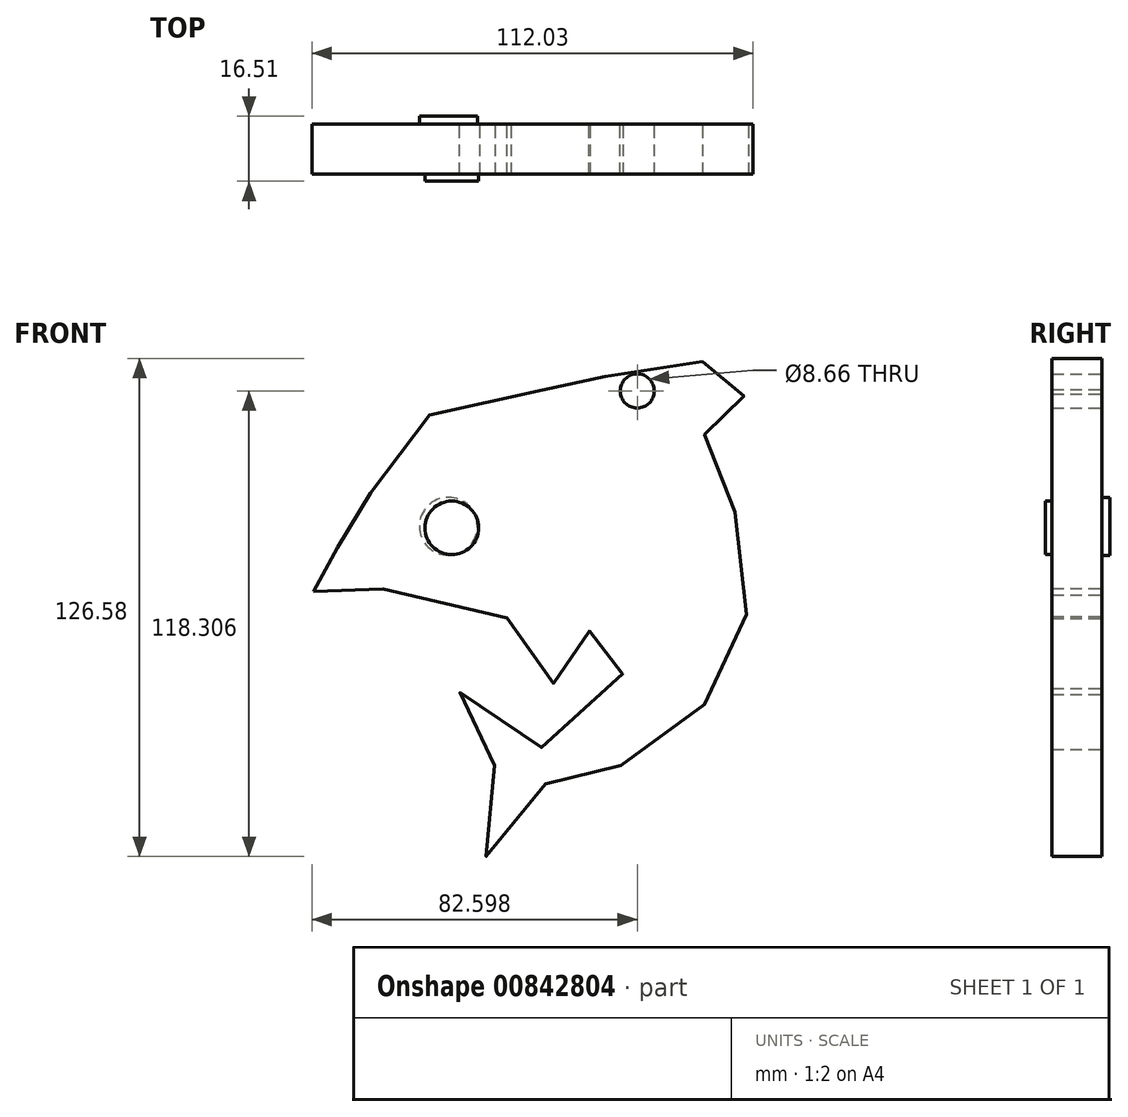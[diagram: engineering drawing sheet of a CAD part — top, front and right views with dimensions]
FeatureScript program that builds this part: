
annotation { "Feature Type Name" : "Feature", "Feature Type Description" : "" }
export const myFeature = defineFeature(function(context is Context, id is Id, definition is map)
    precondition{}
    {
        {
            var Q0;
            Q0=qCreatedBy(makeId("Front.planeOp"),FACE);
            var sketch = newSketch(context, id + "F0", { "sketchPlane" : qUnion([Q0])});
            skFitSpline(sketch, "E0", {"points": [v(-59.96, 0) * mm, v(-59.42, 4.46) * mm, v(-58.6, 5) * mm, v(-52.4, 12.57) * mm, v(-46.17, 17.7) * mm, v(-44.82, 29.6) * mm, v(-29.41, 45.28) * mm, v(-2.92, 51.22) * mm, v(9.5, 50.41) * mm, v(14.65, 55) * mm, v(33.57, 59.06) * mm, v(50.87, 53.39) * mm, v(51.14, 50.68) * mm, v(41.95, 46.36) * mm, v(40.6, 43.65) * mm, v(38.97, 35.27) * mm, v(46.54, 21.22) * mm, v(50.6, 0) * mm, v(45.73, -19.33) * mm, v(32.21, -35.82) * mm, v(13.56, -45.55) * mm, v(0, -47.44) * mm, v(-3.2, -54.74) * mm, v(-17.25, -67.17) * mm, v(-13.74, -45.55) * mm, v(-18.6, -38.79) * mm, v(-22.39, -24.73) * mm, v(-2.38, -39.6) * mm, v(18.7, -24.73) * mm, v(10.6, -6.35) * mm, v(10.32, -14.73) * mm, v(5.18, -26.08) * mm, v(-10.76, -6.62) * mm, v(-9.68, -6.9) * mm, v(-38.33, 0) * mm, v(-49.96, 0) * mm, v(-59.96, 0) * mm]});
            skSolve(sketch);
        }
        {
            var Q0;
            Q0=makeQuery(id+"F0.imprint","IMPRINT",FACE,{"disambiguationData":[TD([[makeQuery(id+"F0.imprint","IMPRINT",EDGE,{"derivedFrom":sQuery(id+"F0.wireOp",EDGE,"E0")}),-1.0]])]});
            extrude(context, id + "F1", {"entities" : qUnion([Q0]), "depth" : 12.7 * mm, "offsetDistance" : 25.4 * mm});
        }
        {
            var Q0;
            Q0=qCreatedBy(makeId("Front.planeOp"),FACE);
            var sketch = newSketch(context, id + "F2", { "sketchPlane" : qUnion([Q0])});
            skCircle(sketch, "E1", {"center": v(-24.86, 16.1) * mm, "radius": 6.8 * mm});
            skSolve(sketch);
        }
        {
            var Q0;
            Q0=makeQuery(id+"F2.imprint","IMPRINT",FACE,{"disambiguationData":[TD([[makeQuery(id+"F2.imprint","IMPRINT",EDGE,{"derivedFrom":sQuery(id+"F2.wireOp",EDGE,"E1")}),1.0]])]});
            extrude(context, id + "F3", {"entities" : qUnion([Q0]), "operationType" : NewBodyOperationType.ADD, "depth" : 14.48 * mm, "offsetDistance" : 25.4 * mm});
        }
        {
            var Q0;
            Q0=qCreatedBy(makeId("Front.planeOp"),FACE);
            var sketch = newSketch(context, id + "F4", { "sketchPlane" : qUnion([Q0])});
            skCircle(sketch, "E2", {"center": v(22.26, 50.89) * mm, "radius": 4.33 * mm});
            skSolve(sketch);
        }
        {
            var Q0;
            Q0=makeQuery(id+"F4.imprint","IMPRINT",FACE,{"disambiguationData":[TD([[makeQuery(id+"F4.imprint","IMPRINT",EDGE,{"derivedFrom":sQuery(id+"F4.wireOp",EDGE,"E2")}),1.0]])]});
            extrude(context, id + "F5", {"entities" : qUnion([Q0]), "operationType" : NewBodyOperationType.REMOVE, "depth" : 19.56 * mm, "offsetDistance" : 25.4 * mm});
        }
        {
            var Q0;
            Q0=qCreatedBy(makeId("Front.planeOp"),FACE);
            var sketch = newSketch(context, id + "F6", { "sketchPlane" : qUnion([Q0])});
            skCircle(sketch, "E3", {"center": v(-25.72, 16.5) * mm, "radius": 7.37 * mm});
            skSolve(sketch);
        }
        {
            var Q0;
            Q0=makeQuery(id+"F6.imprint","IMPRINT",FACE,{"disambiguationData":[TD([[makeQuery(id+"F6.imprint","IMPRINT",EDGE,{"derivedFrom":sQuery(id+"F6.wireOp",EDGE,"E3")}),1.0]])]});
            extrude(context, id + "F7", {"entities" : qUnion([Q0]), "operationType" : NewBodyOperationType.ADD, "oppositeDirection" : true, "depth" : 2.03 * mm, "offsetDistance" : 25.4 * mm});
        }
    });
